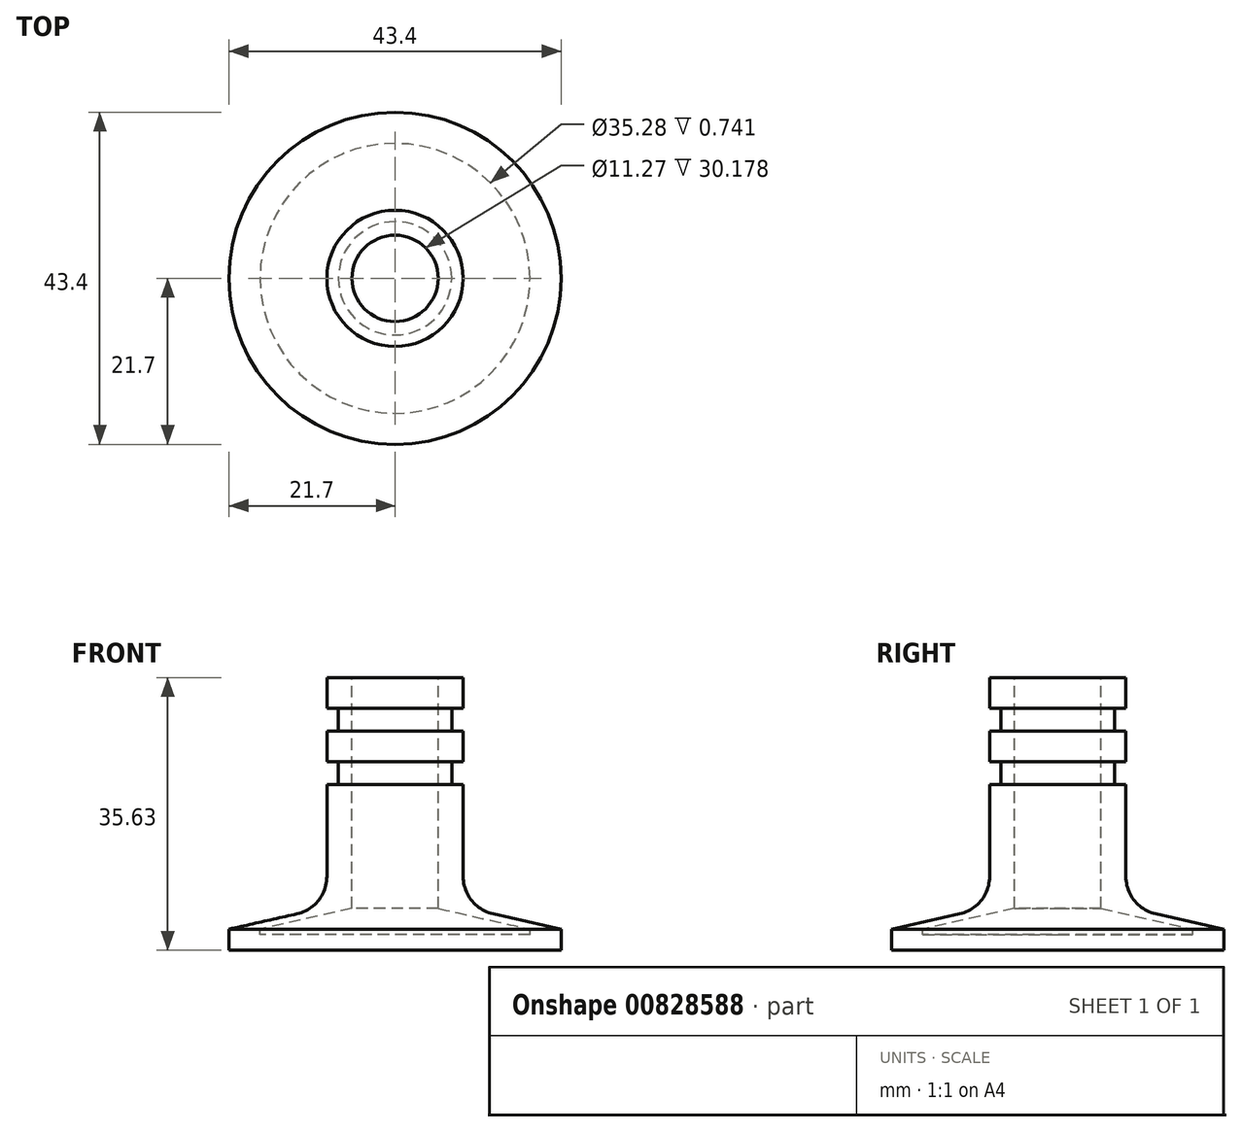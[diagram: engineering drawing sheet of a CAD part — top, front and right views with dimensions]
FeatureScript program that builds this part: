
annotation { "Feature Type Name" : "Feature", "Feature Type Description" : "" }
export const myFeature = defineFeature(function(context is Context, id is Id, definition is map)
    precondition{}
    {
        {
            var Q0;
            Q0=qCreatedBy(makeId("Front.planeOp"),FACE);
            var sketch = newSketch(context, id + "F0", { "sketchPlane" : qUnion([Q0])});
            skLineSegment(sketch, "E0", {"start": v(0, 0) * mm, "end": v(-21.7, 0) * mm});
            skLineSegment(sketch, "E1", {"start": v(-21.7, 0) * mm, "end": v(-21.7, 2.74) * mm});
            skLineSegment(sketch, "E2", {"start": v(-21.7, 2.74) * mm, "end": v(-8.9, 5.63) * mm});
            skLineSegment(sketch, "E3", {"start": v(-8.9, 5.63) * mm, "end": v(-8.9, 21.63) * mm});
            skLineSegment(sketch, "E4", {"start": v(-8.9, 21.63) * mm, "end": v(-7.4, 21.63) * mm});
            skLineSegment(sketch, "E5", {"start": v(-7.4, 21.63) * mm, "end": v(-7.4, 24.63) * mm});
            skLineSegment(sketch, "E6", {"start": v(-7.4, 24.63) * mm, "end": v(-8.9, 24.63) * mm});
            skLineSegment(sketch, "E7", {"start": v(-8.9, 24.63) * mm, "end": v(-8.9, 28.63) * mm});
            skLineSegment(sketch, "E8", {"start": v(-8.9, 28.63) * mm, "end": v(-7.4, 28.63) * mm});
            skLineSegment(sketch, "E9", {"start": v(-7.4, 28.63) * mm, "end": v(-7.4, 31.63) * mm});
            skLineSegment(sketch, "E10", {"start": v(-7.4, 31.63) * mm, "end": v(-8.9, 31.63) * mm});
            skLineSegment(sketch, "E11", {"start": v(-8.9, 31.63) * mm, "end": v(-8.9, 35.63) * mm});
            skLineSegment(sketch, "E12", {"start": v(-8.9, 35.63) * mm, "end": v(-5.64, 35.63) * mm});
            skLineSegment(sketch, "E13", {"start": v(-5.64, 35.63) * mm, "end": v(0, 35.63) * mm, "construction": true});
            skLineSegment(sketch, "E14", {"start": v(-5.64, 35.63) * mm, "end": v(-5.64, 5.46) * mm});
            skLineSegment(sketch, "E15", {"start": v(-5.64, 5.46) * mm, "end": v(-17.64, 2.74) * mm});
            skLineSegment(sketch, "E16", {"start": v(-17.64, 2.74) * mm, "end": v(-17.64, 2) * mm});
            skLineSegment(sketch, "E17", {"start": v(-17.64, 2) * mm, "end": v(0, 2) * mm});
            skLineSegment(sketch, "E18", {"start": v(0, 2) * mm, "end": v(0, 0) * mm});
            skSolve(sketch);
        }
        {
            var Q0;
            Q0=makeQuery(id+"F0.imprint","IMPRINT",FACE,{"disambiguationData":[TD([[makeQuery(id+"F0.imprint","IMPRINT",EDGE,{"derivedFrom":sQuery(id+"F0.wireOp",EDGE,"E0")}),-1.0]])]});
            var sketch = newSketch(context, id + "F1", { "sketchPlane" : qUnion([Q0])});
            skLineSegment(sketch, "E19", {"start": v(0, 35.7) * mm, "end": v(0, 1.96) * mm});
            skSolve(sketch);
        }
        {
            var Q0;
            Q0 = qSketchRegion(id + "F0", true);
            var Q1;
            Q1=sQuery(id+"F1.wireOp",EDGE,"E19");
            revolve(context, id + "F2", {"surfaceOperationType" : NewSurfaceOperationType.NEW, "entities" : qUnion([Q0]), "axis" : qUnion([Q1]), "revolveType" : RevolveType.FULL});
        }
        {
            var Q0;
            Q0=makeQuery(id+"F2.opRevolve","SWEPT_EDGE",EDGE,{"disambiguationData":[OSD([sQuery(id+"F0.wireOp",EDGE,"E2"),sQuery(id+"F0.wireOp",EDGE,"E3")])]});
            fillet(context, id + "F3", {"entities" : qUnion([Q0]), "radius" : 5 * mm, "tangentPropagation" : true, "allowEdgeOverflow" : false});
        }
    });
